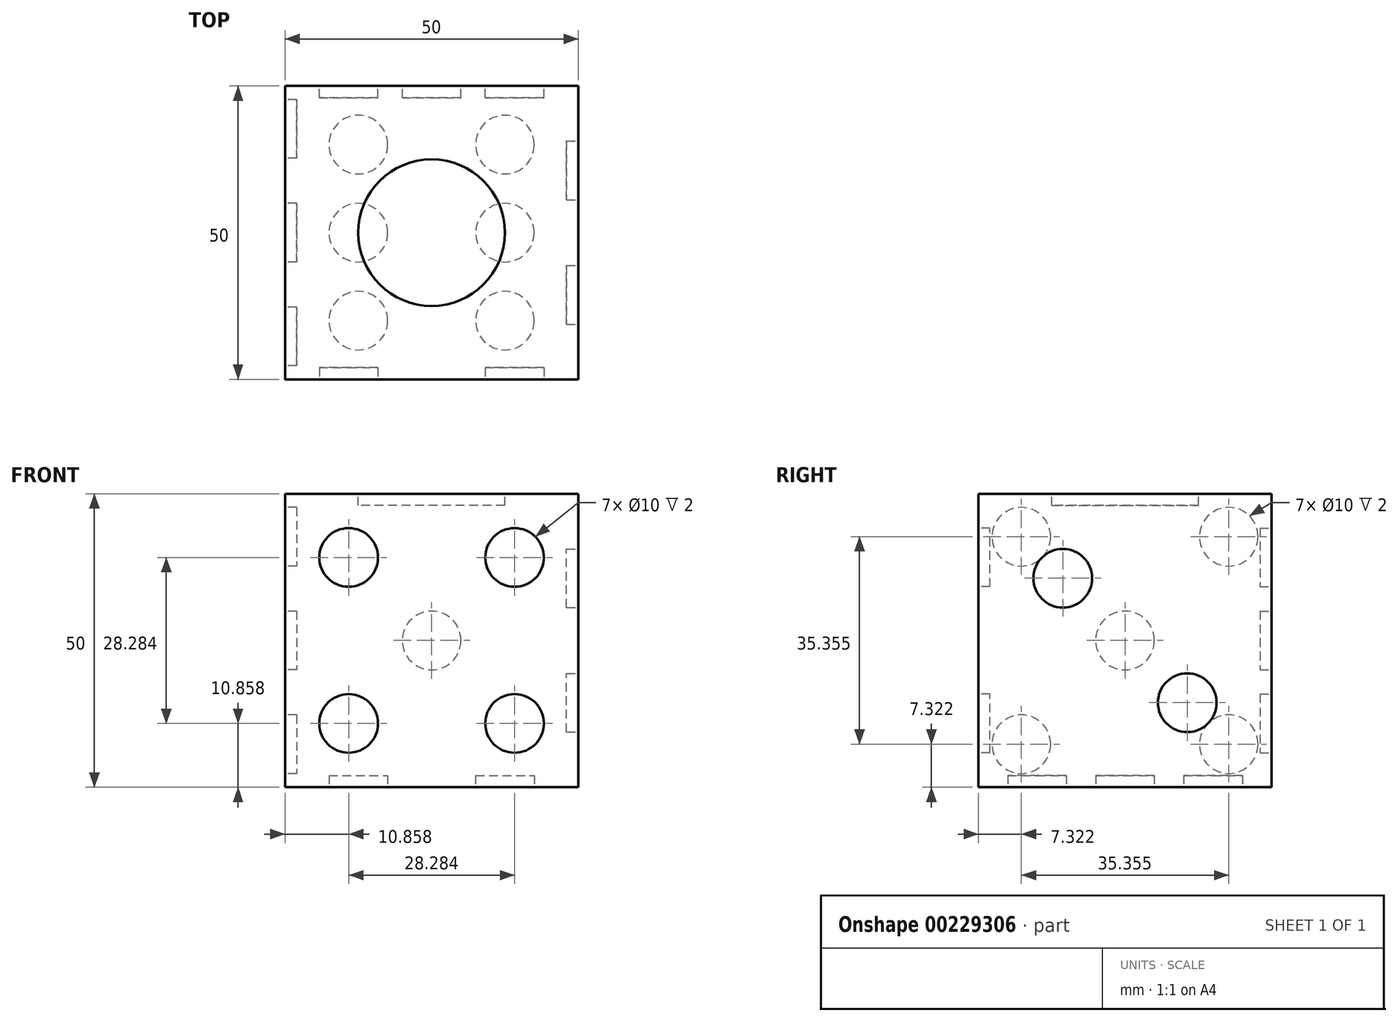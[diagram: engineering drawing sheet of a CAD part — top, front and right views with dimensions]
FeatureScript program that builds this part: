
annotation { "Feature Type Name" : "Feature", "Feature Type Description" : "" }
export const myFeature = defineFeature(function(context is Context, id is Id, definition is map)
    precondition{}
    {
        {
            var Q0;
            Q0=qCreatedBy(makeId("Top.planeOp"),FACE);
            var sketch = newSketch(context, id + "F0", { "sketchPlane" : qUnion([Q0])});
            skLineSegment(sketch, "E0.bottom", {"start": v(-25, 25) * mm, "end": v(25, 25) * mm});
            skLineSegment(sketch, "E0.top", {"start": v(-25, -25) * mm, "end": v(25, -25) * mm});
            skLineSegment(sketch, "E0.left", {"start": v(-25, 25) * mm, "end": v(-25, -25) * mm});
            skLineSegment(sketch, "E0.right", {"start": v(25, 25) * mm, "end": v(25, -25) * mm});
            skPoint(sketch, "E1", {"position": v(0, 25) * mm});
            skPoint(sketch, "E2", {"position": v(25, 0) * mm});
            skSolve(sketch);
        }
        {
            var Q0;
            Q0=makeQuery(id+"F0.imprint","IMPRINT",FACE,{"disambiguationData":[TD([[makeQuery(id+"F0.imprint","IMPRINT",EDGE,{"derivedFrom":sQuery(id+"F0.wireOp",EDGE,"E0.bottom")}),-1.0]])]});
            extrude(context, id + "F1", {"entities" : qUnion([Q0]), "depth" : 50 * mm});
        }
        {
            var Q0;
            Q0=makeQuery(id+"F1.opExtrude","CAP_FACE",FACE,{"disambiguationData":[OSD([sQuery(id+"F0.wireOp",EDGE,"E0.bottom"),sQuery(id+"F0.wireOp",EDGE,"E0.top"),sQuery(id+"F0.wireOp",EDGE,"E0.left"),sQuery(id+"F0.wireOp",EDGE,"E0.right")])],"isStart":false});
            var sketch = newSketch(context, id + "F2", { "sketchPlane" : qUnion([Q0])});
            skCircle(sketch, "E3", {"center": v(0, 0) * mm, "radius": 12.5 * mm});
            skSolve(sketch);
        }
        {
            var Q0;
            Q0=makeQuery(id+"F2.imprint","IMPRINT",FACE,{"disambiguationData":[TD([[makeQuery(id+"F2.imprint","IMPRINT",EDGE,{"derivedFrom":sQuery(id+"F2.wireOp",EDGE,"E3")}),1.0]])]});
            extrude(context, id + "F3", {"entities" : qUnion([Q0]), "operationType" : NewBodyOperationType.REMOVE, "oppositeDirection" : true, "depth" : 2 * mm});
        }
        {
            var Q0;
            Q0=makeQuery(id+"F1.opExtrude","SWEPT_FACE",FACE,{"disambiguationData":[OSD([sQuery(id+"F0.wireOp",EDGE,"E0.right")])]});
            var sketch = newSketch(context, id + "F4", { "sketchPlane" : qUnion([Q0])});
            skCircle(sketch, "E4", {"center": v(-10.6, 35.6) * mm, "radius": 5 * mm});
            skCircle(sketch, "E5", {"center": v(10.6, 14.4) * mm, "radius": 5 * mm});
            skLineSegment(sketch, "E6", {"start": v(-25, 50) * mm, "end": v(25, 0) * mm, "construction": true});
            skLineSegment(sketch, "E7", {"start": v(-10.6, 35.6) * mm, "end": v(10.6, 14.4) * mm, "construction": true});
            skPoint(sketch, "E8", {"position": v(0, 25) * mm});
            skSolve(sketch);
        }
        {
            var Q0;
            Q0=makeQuery(id+"F4.imprint","IMPRINT",FACE,{"disambiguationData":[TD([[makeQuery(id+"F4.imprint","IMPRINT",EDGE,{"derivedFrom":sQuery(id+"F4.wireOp",EDGE,"E4")}),1.0]])]});
            var Q1;
            Q1=makeQuery(id+"F4.imprint","IMPRINT",FACE,{"disambiguationData":[TD([[makeQuery(id+"F4.imprint","IMPRINT",EDGE,{"derivedFrom":sQuery(id+"F4.wireOp",EDGE,"E5")}),1.0]])]});
            extrude(context, id + "F5", {"entities" : qUnion([Q0, Q1]), "operationType" : NewBodyOperationType.REMOVE, "oppositeDirection" : true, "depth" : 2 * mm});
        }
        {
            var Q0;
            Q0=makeQuery(id+"F1.opExtrude","SWEPT_FACE",FACE,{"disambiguationData":[OSD([sQuery(id+"F0.wireOp",EDGE,"E0.bottom")])]});
            var sketch = newSketch(context, id + "F6", { "sketchPlane" : qUnion([Q0])});
            skLineSegment(sketch, "E9", {"start": v(-25, 50) * mm, "end": v(25, 0) * mm, "construction": true});
            skCircle(sketch, "E10", {"center": v(-14.14, 39.14) * mm, "radius": 5 * mm});
            skCircle(sketch, "E11", {"center": v(0, 25) * mm, "radius": 5 * mm});
            skCircle(sketch, "E12", {"center": v(14.14, 10.86) * mm, "radius": 5 * mm});
            skLineSegment(sketch, "E13", {"start": v(-14.14, 39.14) * mm, "end": v(0, 25) * mm, "construction": true});
            skLineSegment(sketch, "E14", {"start": v(0, 25) * mm, "end": v(14.14, 10.86) * mm, "construction": true});
            skSolve(sketch);
        }
        {
            var Q0;
            Q0=makeQuery(id+"F6.imprint","IMPRINT",FACE,{"disambiguationData":[TD([[makeQuery(id+"F6.imprint","IMPRINT",EDGE,{"derivedFrom":sQuery(id+"F6.wireOp",EDGE,"E11")}),1.0]])]});
            var Q1;
            Q1=makeQuery(id+"F6.imprint","IMPRINT",FACE,{"disambiguationData":[TD([[makeQuery(id+"F6.imprint","IMPRINT",EDGE,{"derivedFrom":sQuery(id+"F6.wireOp",EDGE,"E10")}),1.0]])]});
            var Q2;
            Q2=makeQuery(id+"F6.imprint","IMPRINT",FACE,{"disambiguationData":[TD([[makeQuery(id+"F6.imprint","IMPRINT",EDGE,{"derivedFrom":sQuery(id+"F6.wireOp",EDGE,"E12")}),1.0]])]});
            extrude(context, id + "F7", {"entities" : qUnion([Q0, Q1, Q2]), "operationType" : NewBodyOperationType.REMOVE, "oppositeDirection" : true, "depth" : 2 * mm});
        }
        {
            var Q0;
            Q0=makeQuery(id+"F1.opExtrude","SWEPT_FACE",FACE,{"disambiguationData":[OSD([sQuery(id+"F0.wireOp",EDGE,"E0.top")])]});
            var sketch = newSketch(context, id + "F8", { "sketchPlane" : qUnion([Q0])});
            skLineSegment(sketch, "E15", {"start": v(-25, 50) * mm, "end": v(25, 0) * mm, "construction": true});
            skLineSegment(sketch, "E16", {"start": v(25, 50) * mm, "end": v(-25, 0) * mm, "construction": true});
            skCircle(sketch, "E17", {"center": v(-14.14, 39.14) * mm, "radius": 5 * mm});
            skCircle(sketch, "E18", {"center": v(14.14, 39.14) * mm, "radius": 5 * mm});
            skCircle(sketch, "E19", {"center": v(-14.14, 10.86) * mm, "radius": 5 * mm});
            skCircle(sketch, "E20", {"center": v(14.14, 10.86) * mm, "radius": 5 * mm});
            skLineSegment(sketch, "E21", {"start": v(-14.14, 39.14) * mm, "end": v(14.14, 10.86) * mm, "construction": true});
            skLineSegment(sketch, "E22", {"start": v(14.14, 39.14) * mm, "end": v(-14.14, 10.86) * mm, "construction": true});
            skSolve(sketch);
        }
        {
            var Q0;
            Q0=makeQuery(id+"F8.imprint","IMPRINT",FACE,{"disambiguationData":[TD([[makeQuery(id+"F8.imprint","IMPRINT",EDGE,{"derivedFrom":sQuery(id+"F8.wireOp",EDGE,"E18")}),1.0]])]});
            var Q1;
            Q1=makeQuery(id+"F8.imprint","IMPRINT",FACE,{"disambiguationData":[TD([[makeQuery(id+"F8.imprint","IMPRINT",EDGE,{"derivedFrom":sQuery(id+"F8.wireOp",EDGE,"E17")}),1.0]])]});
            var Q2;
            Q2=makeQuery(id+"F8.imprint","IMPRINT",FACE,{"disambiguationData":[TD([[makeQuery(id+"F8.imprint","IMPRINT",EDGE,{"derivedFrom":sQuery(id+"F8.wireOp",EDGE,"E19")}),1.0]])]});
            var Q3;
            Q3=makeQuery(id+"F8.imprint","IMPRINT",FACE,{"disambiguationData":[TD([[makeQuery(id+"F8.imprint","IMPRINT",EDGE,{"derivedFrom":sQuery(id+"F8.wireOp",EDGE,"E20")}),1.0]])]});
            extrude(context, id + "F9", {"entities" : qUnion([Q0, Q1, Q2, Q3]), "operationType" : NewBodyOperationType.REMOVE, "oppositeDirection" : true, "depth" : 2 * mm});
        }
        {
            var Q0;
            Q0=makeQuery(id+"F1.opExtrude","SWEPT_FACE",FACE,{"disambiguationData":[OSD([sQuery(id+"F0.wireOp",EDGE,"E0.left")])]});
            var sketch = newSketch(context, id + "F10", { "sketchPlane" : qUnion([Q0])});
            skLineSegment(sketch, "E23", {"start": v(-25, 50) * mm, "end": v(25, 0) * mm, "construction": true});
            skLineSegment(sketch, "E24", {"start": v(-25, 0) * mm, "end": v(25, 50) * mm, "construction": true});
            skCircle(sketch, "E25", {"center": v(0, 25) * mm, "radius": 5 * mm});
            skCircle(sketch, "E26", {"center": v(17.68, 42.68) * mm, "radius": 5 * mm});
            skCircle(sketch, "E27", {"center": v(-17.68, 42.68) * mm, "radius": 5 * mm});
            skCircle(sketch, "E28", {"center": v(-17.68, 7.32) * mm, "radius": 5 * mm});
            skCircle(sketch, "E29", {"center": v(17.68, 7.32) * mm, "radius": 5 * mm});
            skLineSegment(sketch, "E30", {"start": v(-17.68, 42.68) * mm, "end": v(0, 25) * mm, "construction": true});
            skLineSegment(sketch, "E31", {"start": v(17.68, 7.32) * mm, "end": v(0, 25) * mm, "construction": true});
            skLineSegment(sketch, "E32", {"start": v(-17.68, 7.32) * mm, "end": v(0, 25) * mm, "construction": true});
            skLineSegment(sketch, "E33", {"start": v(0, 25) * mm, "end": v(17.68, 42.68) * mm, "construction": true});
            skSolve(sketch);
        }
        {
            var Q0;
            Q0=makeQuery(id+"F10.imprint","IMPRINT",FACE,{"disambiguationData":[TD([[makeQuery(id+"F10.imprint","IMPRINT",EDGE,{"derivedFrom":sQuery(id+"F10.wireOp",EDGE,"E27")}),1.0]])]});
            var Q1;
            Q1=makeQuery(id+"F10.imprint","IMPRINT",FACE,{"disambiguationData":[TD([[makeQuery(id+"F10.imprint","IMPRINT",EDGE,{"derivedFrom":sQuery(id+"F10.wireOp",EDGE,"E25")}),1.0]])]});
            var Q2;
            Q2=makeQuery(id+"F10.imprint","IMPRINT",FACE,{"disambiguationData":[TD([[makeQuery(id+"F10.imprint","IMPRINT",EDGE,{"derivedFrom":sQuery(id+"F10.wireOp",EDGE,"E28")}),1.0]])]});
            var Q3;
            Q3=makeQuery(id+"F10.imprint","IMPRINT",FACE,{"disambiguationData":[TD([[makeQuery(id+"F10.imprint","IMPRINT",EDGE,{"derivedFrom":sQuery(id+"F10.wireOp",EDGE,"E29")}),1.0]])]});
            var Q4;
            Q4=makeQuery(id+"F10.imprint","IMPRINT",FACE,{"disambiguationData":[TD([[makeQuery(id+"F10.imprint","IMPRINT",EDGE,{"derivedFrom":sQuery(id+"F10.wireOp",EDGE,"E26")}),1.0]])]});
            extrude(context, id + "F11", {"entities" : qUnion([Q0, Q1, Q2, Q3, Q4]), "operationType" : NewBodyOperationType.REMOVE, "oppositeDirection" : true, "depth" : 2 * mm});
        }
        {
            var Q0;
            Q0=makeQuery(id+"F1.opExtrude","CAP_FACE",FACE,{"disambiguationData":[OSD([sQuery(id+"F0.wireOp",EDGE,"E0.bottom"),sQuery(id+"F0.wireOp",EDGE,"E0.top"),sQuery(id+"F0.wireOp",EDGE,"E0.left"),sQuery(id+"F0.wireOp",EDGE,"E0.right")])],"isStart":true});
            var sketch = newSketch(context, id + "F12", { "sketchPlane" : qUnion([Q0])});
            skLineSegment(sketch, "E34", {"start": v(-25, 25) * mm, "end": v(0, 25) * mm, "construction": true});
            skLineSegment(sketch, "E35", {"start": v(0, 25) * mm, "end": v(25, 25) * mm, "construction": true});
            skLineSegment(sketch, "E36", {"start": v(-25, -25) * mm, "end": v(0, -25) * mm, "construction": true});
            skLineSegment(sketch, "E37", {"start": v(0, -25) * mm, "end": v(25, -25) * mm, "construction": true});
            skPoint(sketch, "E38", {"position": v(-12.5, 25) * mm});
            skPoint(sketch, "E39", {"position": v(-12.5, -25) * mm});
            skPoint(sketch, "E40", {"position": v(12.5, -25) * mm});
            skPoint(sketch, "E41", {"position": v(12.5, 25) * mm});
            skLineSegment(sketch, "E42", {"start": v(12.5, 25) * mm, "end": v(12.5, -25) * mm, "construction": true});
            skLineSegment(sketch, "E43", {"start": v(-12.5, 25) * mm, "end": v(-12.5, -25) * mm, "construction": true});
            skLineSegment(sketch, "E44", {"start": v(-12.5, 15) * mm, "end": v(-12.5, 0) * mm, "construction": true});
            skLineSegment(sketch, "E45", {"start": v(-12.5, -15) * mm, "end": v(-12.5, 0) * mm, "construction": true});
            skCircle(sketch, "E46", {"center": v(-12.5, 15) * mm, "radius": 5 * mm});
            skCircle(sketch, "E47", {"center": v(-12.5, 0) * mm, "radius": 5 * mm});
            skCircle(sketch, "E48", {"center": v(-12.5, -15) * mm, "radius": 5 * mm});
            skCircle(sketch, "E49", {"center": v(12.5, -15) * mm, "radius": 5 * mm});
            skCircle(sketch, "E50", {"center": v(12.5, 0) * mm, "radius": 5 * mm});
            skCircle(sketch, "E51", {"center": v(12.5, 15) * mm, "radius": 5 * mm});
            skSolve(sketch);
        }
        {
            var Q0;
            Q0=makeQuery(id+"F12.imprint","IMPRINT",FACE,{"disambiguationData":[TD([[makeQuery(id+"F12.imprint","IMPRINT",EDGE,{"derivedFrom":sQuery(id+"F12.wireOp",EDGE,"E46")}),1.0]])]});
            var Q1;
            Q1=makeQuery(id+"F12.imprint","IMPRINT",FACE,{"disambiguationData":[TD([[makeQuery(id+"F12.imprint","IMPRINT",EDGE,{"derivedFrom":sQuery(id+"F12.wireOp",EDGE,"E47")}),1.0]])]});
            var Q2;
            Q2=makeQuery(id+"F12.imprint","IMPRINT",FACE,{"disambiguationData":[TD([[makeQuery(id+"F12.imprint","IMPRINT",EDGE,{"derivedFrom":sQuery(id+"F12.wireOp",EDGE,"E48")}),1.0]])]});
            var Q3;
            Q3=makeQuery(id+"F12.imprint","IMPRINT",FACE,{"disambiguationData":[TD([[makeQuery(id+"F12.imprint","IMPRINT",EDGE,{"derivedFrom":sQuery(id+"F12.wireOp",EDGE,"E49")}),1.0]])]});
            var Q4;
            Q4=makeQuery(id+"F12.imprint","IMPRINT",FACE,{"disambiguationData":[TD([[makeQuery(id+"F12.imprint","IMPRINT",EDGE,{"derivedFrom":sQuery(id+"F12.wireOp",EDGE,"E50")}),1.0]])]});
            var Q5;
            Q5=makeQuery(id+"F12.imprint","IMPRINT",FACE,{"disambiguationData":[TD([[makeQuery(id+"F12.imprint","IMPRINT",EDGE,{"derivedFrom":sQuery(id+"F12.wireOp",EDGE,"E51")}),1.0]])]});
            extrude(context, id + "F13", {"entities" : qUnion([Q0, Q1, Q2, Q3, Q4, Q5]), "operationType" : NewBodyOperationType.REMOVE, "oppositeDirection" : true, "depth" : 2 * mm});
        }
    });
